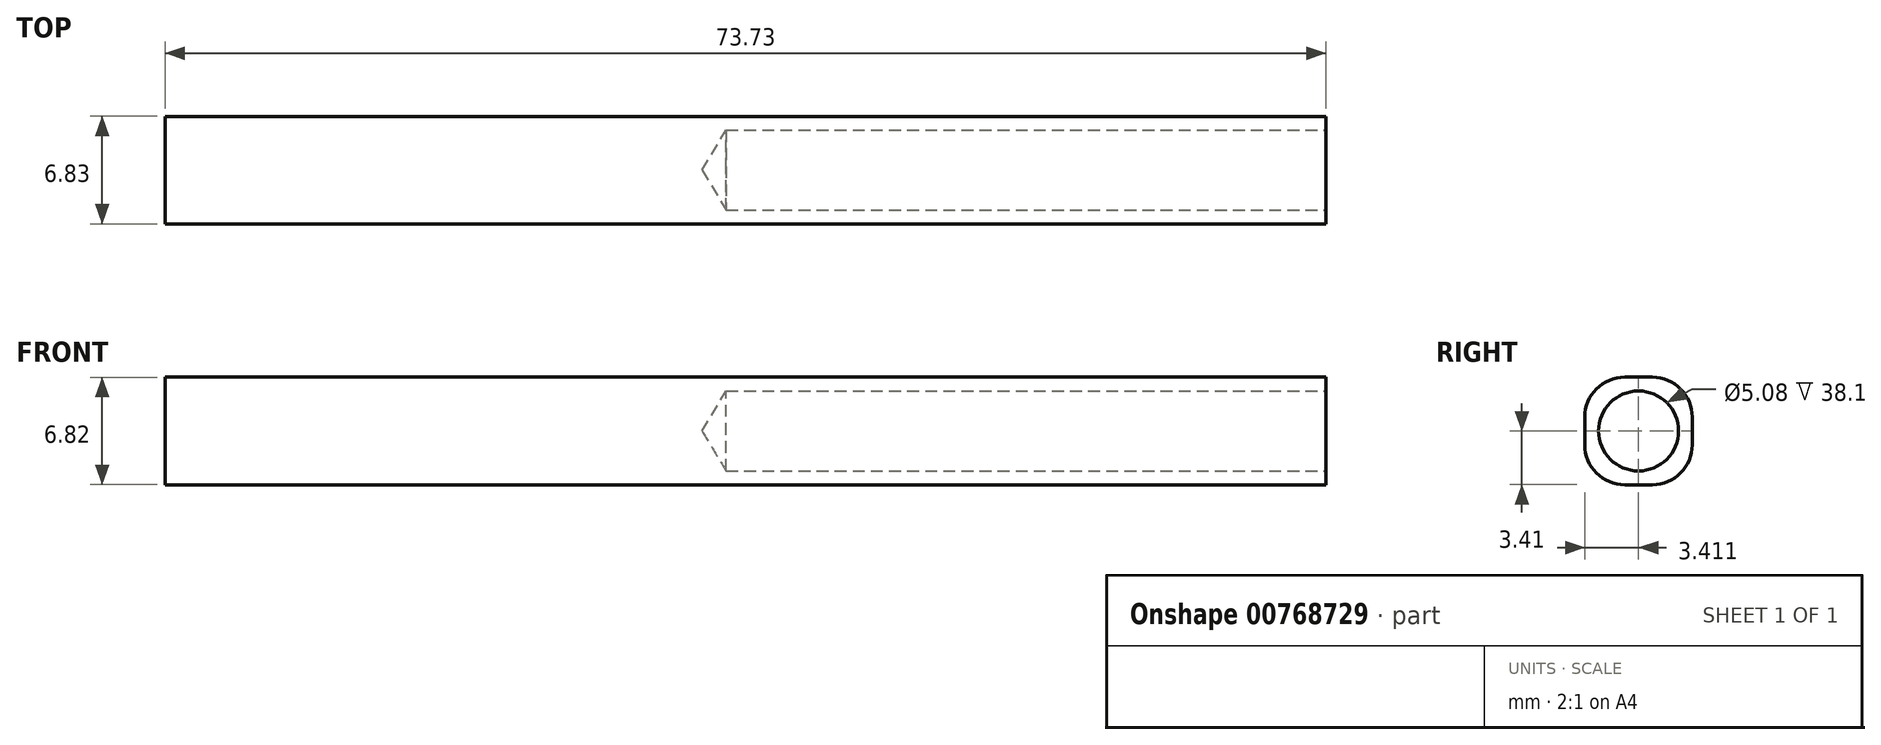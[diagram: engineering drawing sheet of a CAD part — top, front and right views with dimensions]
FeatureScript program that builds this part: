
annotation { "Feature Type Name" : "Feature", "Feature Type Description" : "" }
export const myFeature = defineFeature(function(context is Context, id is Id, definition is map)
    precondition{}
    {
        {
            var Q0;
            Q0=qCreatedBy(makeId("Top.planeOp"),FACE);
            var sketch = newSketch(context, id + "F0", { "sketchPlane" : qUnion([Q0])});
            skPoint(sketch, "E0.middle", {"position": v(0, 0) * mm});
            skLineSegment(sketch, "E1", {"start": v(-56.4, 37.8) * mm, "end": v(4.07, 37.8) * mm});
            skLineSegment(sketch, "E2", {"start": v(4.07, 37.8) * mm, "end": v(8.26, 33.99) * mm});
            skLineSegment(sketch, "E3", {"start": v(8.26, 33.99) * mm, "end": v(81.99, 33.99) * mm});
            skLineSegment(sketch, "E4", {"start": v(81.99, 27.16) * mm, "end": v(8.26, 27.16) * mm});
            skLineSegment(sketch, "E5", {"start": v(8.26, 27.16) * mm, "end": v(8.26, 33.99) * mm});
            skLineSegment(sketch, "E6", {"start": v(81.99, 33.99) * mm, "end": v(81.99, 27.16) * mm});
            skLineSegment(sketch, "E7", {"start": v(8.26, 27.16) * mm, "end": v(-36.4, 22.27) * mm});
            skLineSegment(sketch, "E8", {"start": v(-32.67, 22.68) * mm, "end": v(4.07, 22.68) * mm});
            skLineSegment(sketch, "E9", {"start": v(4.07, 22.68) * mm, "end": v(3.58, 27.16) * mm});
            skLineSegment(sketch, "E10", {"start": v(4.07, 22.68) * mm, "end": v(62.68, 27.16) * mm});
            skLineSegment(sketch, "E11", {"start": v(58.85, 33.99) * mm, "end": v(51.25, 37.8) * mm});
            skLineSegment(sketch, "E12", {"start": v(51.02, 33.99) * mm, "end": v(43.43, 37.8) * mm});
            skLineSegment(sketch, "E13", {"start": v(43.2, 33.99) * mm, "end": v(35.6, 37.8) * mm});
            skLineSegment(sketch, "E14", {"start": v(35.38, 33.99) * mm, "end": v(27.78, 37.8) * mm});
            skLineSegment(sketch, "E15", {"start": v(27.55, 33.99) * mm, "end": v(19.96, 37.8) * mm});
            skLineSegment(sketch, "E16", {"start": v(4.07, 37.8) * mm, "end": v(51.25, 37.8) * mm});
            skLineSegment(sketch, "E17", {"start": v(78.08, 33.99) * mm, "end": v(78.74, 44.53) * mm});
            skLineSegment(sketch, "E18", {"start": v(78.74, 44.53) * mm, "end": v(71.37, 43.97) * mm});
            skLineSegment(sketch, "E19", {"start": v(71.37, 43.97) * mm, "end": v(71.37, 33.99) * mm});
            skLineSegment(sketch, "E20", {"start": v(8.26, 27.16) * mm, "end": v(-42.87, 27.16) * mm});
            skLineSegment(sketch, "E21", {"start": v(-36.41, 27.16) * mm, "end": v(-36.4, 22.27) * mm});
            skLineSegment(sketch, "E22", {"start": v(-42.87, 27.16) * mm, "end": v(-51.08, 12.3) * mm});
            skLineSegment(sketch, "E23", {"start": v(-59.66, 12.3) * mm, "end": v(-51.08, 27.16) * mm});
            skLineSegment(sketch, "E24", {"start": v(-59.66, 12.3) * mm, "end": v(-51.08, 12.3) * mm});
            skLineSegment(sketch, "E25", {"start": v(-42.87, 27.16) * mm, "end": v(-51.08, 27.16) * mm});
            skLineSegment(sketch, "E26", {"start": v(-51.08, 27.16) * mm, "end": v(-60.28, 28.82) * mm});
            skLineSegment(sketch, "E27", {"start": v(-60.28, 28.82) * mm, "end": v(-56.4, 37.8) * mm});
            skLineSegment(sketch, "E28", {"start": v(6.68, 22.88) * mm, "end": v(9.13, 6.81) * mm});
            skLineSegment(sketch, "E29", {"start": v(14.31, 6.81) * mm, "end": v(11.8, 23.27) * mm});
            skLineSegment(sketch, "E30", {"start": v(9.13, 6.81) * mm, "end": v(14.31, 6.81) * mm});
            skLineSegment(sketch, "E31", {"start": v(5.32, 36.66) * mm, "end": v(51.25, 36.66) * mm});
            skLineSegment(sketch, "E32", {"start": v(51.25, 36.66) * mm, "end": v(56.58, 33.99) * mm});
            skLineSegment(sketch, "E33", {"start": v(6.16, 35.9) * mm, "end": v(52.78, 35.9) * mm});
            skLineSegment(sketch, "E34", {"start": v(55.12, 34.72) * mm, "end": v(7.45, 34.72) * mm});
            skLineSegment(sketch, "E35", {"start": v(22.22, 37.8) * mm, "end": v(29.82, 33.99) * mm});
            skLineSegment(sketch, "E36", {"start": v(30.05, 37.8) * mm, "end": v(37.64, 33.99) * mm});
            skLineSegment(sketch, "E37", {"start": v(37.87, 37.8) * mm, "end": v(45.47, 33.99) * mm});
            skLineSegment(sketch, "E38", {"start": v(45.7, 37.8) * mm, "end": v(53.29, 33.99) * mm});
            skLineSegment(sketch, "E39", {"start": v(-36.4, 22.27) * mm, "end": v(-45.58, 22.25) * mm});
            skLineSegment(sketch, "E40", {"start": v(-36.4, 22.74) * mm, "end": v(-45.3, 22.74) * mm});
            skLineSegment(sketch, "E41.bottom", {"start": v(-42.93, 35.37) * mm, "end": v(-23.88, 35.37) * mm});
            skLineSegment(sketch, "E41.top", {"start": v(-42.93, 29.02) * mm, "end": v(-23.88, 29.02) * mm});
            skLineSegment(sketch, "E41.left", {"start": v(-42.93, 35.37) * mm, "end": v(-42.93, 29.02) * mm});
            skLineSegment(sketch, "E41.right", {"start": v(-23.88, 35.37) * mm, "end": v(-23.88, 29.02) * mm});
            skSolve(sketch);
        }
        {
            var Q0;
            {var subQ8=sQuery(id+"F0.wireOp",EDGE,"E5");Q0=makeQuery(id+"F0.imprint","IMPRINT",FACE,{"disambiguationData":[TD([[makeQuery(id+"F0.imprint","IMPRINT",EDGE,{"derivedFrom":subQ8}),-1.0]])]});}
            extrude(context, id + "F1", {"entities" : qUnion([Q0]), "depth" : 6.83 * mm / 2, "offsetDistance" : 25.4 * mm, "hasSecondDirection" : true, "secondDirectionOppositeDirection" : true, "secondDirectionDepth" : 6.83 * mm / 2});
        }
        {
            var Q0;
            Q0=makeQuery(id+"F1.opExtrude","SWEPT_FACE",FACE,{"disambiguationData":[OSD([sQuery(id+"F0.wireOp",EDGE,"E6")])]});
            var sketch = newSketch(context, id + "F2", { "sketchPlane" : qUnion([Q0])});
            skLineSegment(sketch, "E42", {"start": v(33.99, 0) * mm, "end": v(27.16, 0) * mm});
            skPoint(sketch, "E43", {"position": v(30.57, 0) * mm});
            skSolve(sketch);
        }
        {
            var Q0;
            Q0=sQuery(id+"F2.wireOp",VERTEX,"E43");
            var Q1;
            Q1=makeQuery(id+"F1.opExtrude","SWEPT_BODY",BODY,{"disambiguationData":[OSD([sQuery(id+"F0.wireOp",EDGE,"E3"),sQuery(id+"F0.wireOp",EDGE,"E4"),sQuery(id+"F0.wireOp",EDGE,"E5"),sQuery(id+"F0.wireOp",EDGE,"E6")])]});
            hole(context, id + "F3", {"style" : HoleStyle.SIMPLE, "endStyle" : HoleEndStyle.BLIND, "holeDiameter" : 5.08 * mm, "majorDiameter" : 6.35 * mm, "holeDepth" : 38.1 * mm, "isTappedThrough" : true, "tappedDepth" : 12.7 * mm, "tapClearance" : 3, "locations" : qUnion([Q0]), "scope" : qUnion([Q1])});
        }
        {
            var Q0;
            Q0=makeQuery(id+"F1.opExtrude","CAP_EDGE",EDGE,{"disambiguationData":[OSD([sQuery(id+"F0.wireOp",EDGE,"E3")])],"isStart":false});
            var Q1;
            Q1=makeQuery(id+"F1.opExtrude","CAP_EDGE",EDGE,{"disambiguationData":[OSD([sQuery(id+"F0.wireOp",EDGE,"E4")])],"isStart":false});
            var Q2;
            Q2=makeQuery(id+"F1.opExtrude","CAP_EDGE",EDGE,{"disambiguationData":[OSD([sQuery(id+"F0.wireOp",EDGE,"E3")])],"isStart":true});
            var Q3;
            Q3=makeQuery(id+"F1.opExtrude","CAP_EDGE",EDGE,{"disambiguationData":[OSD([sQuery(id+"F0.wireOp",EDGE,"E4")])],"isStart":true});
            fillet(context, id + "F4", {"entities" : qUnion([Q0, Q1, Q2, Q3]), "radius" : 2.54 * mm, "tangentPropagation" : true, "allowEdgeOverflow" : false});
        }
    });
